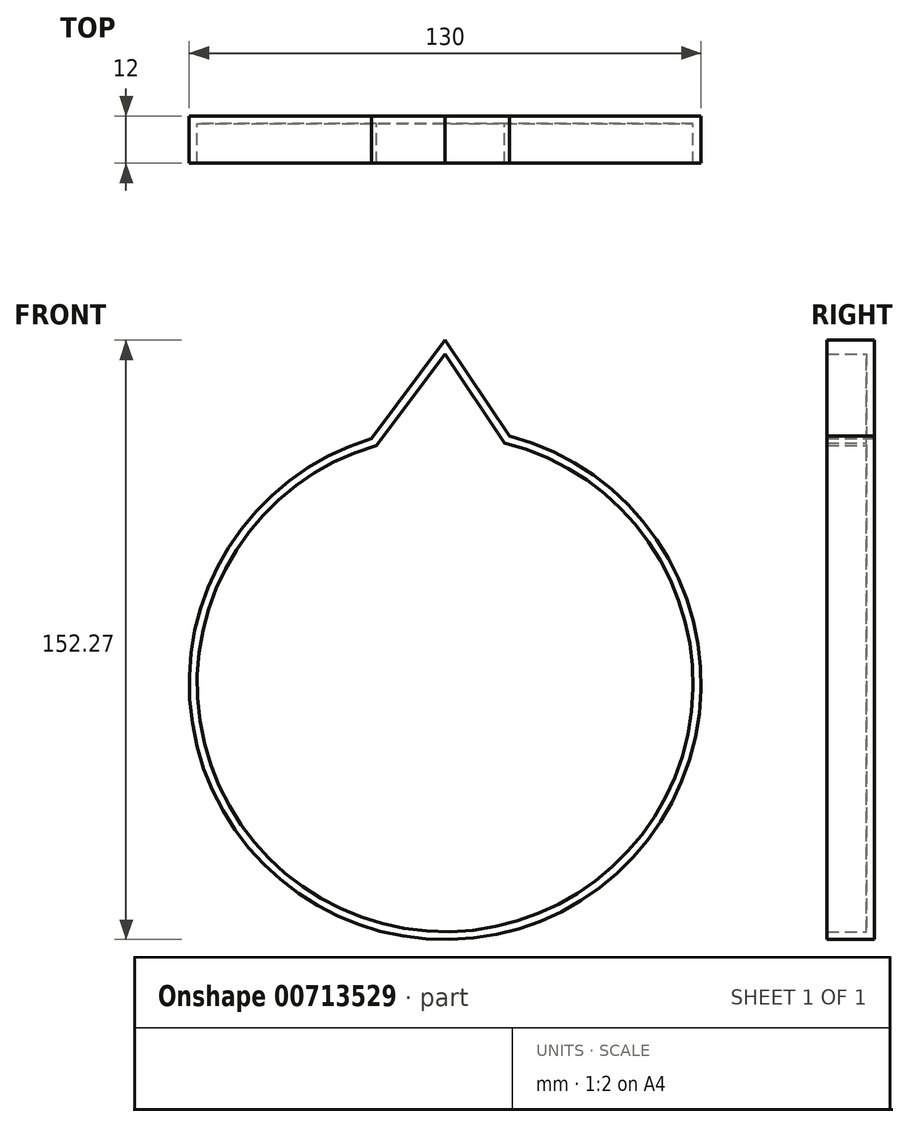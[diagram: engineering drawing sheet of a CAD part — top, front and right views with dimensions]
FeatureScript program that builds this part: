
annotation { "Feature Type Name" : "Feature", "Feature Type Description" : "" }
export const myFeature = defineFeature(function(context is Context, id is Id, definition is map)
    precondition{}
    {
        {
            var Q0;
            Q0=qCreatedBy(makeId("Front.planeOp"),FACE);
            var sketch = newSketch(context, id + "F0", { "sketchPlane" : qUnion([Q0])});
            skArc(sketch, "E0", {"start": v(-18.65, 62.27) * mm, "mid": v(1.2, -64.99) * mm, "end": v(16.35, 62.9) * mm});
            skLineSegment(sketch, "E1", {"start": v(0, 0) * mm, "end": v(0, 87.27) * mm, "construction": true});
            skLineSegment(sketch, "E2", {"start": v(0, 87.27) * mm, "end": v(-18.65, 62.27) * mm});
            skLineSegment(sketch, "E3", {"start": v(16.35, 62.9) * mm, "end": v(0, 87.27) * mm});
            skSolve(sketch);
        }
        {
            var Q0;
            Q0 = qSketchRegion(id + "F0", true);
            extrude(context, id + "F1", {"entities" : qUnion([Q0]), "depth" : 12 * mm, "offsetDistance" : 25 * mm});
        }
        {
            var Q0;
            Q0=makeQuery(id+"F1.opExtrude","CAP_FACE",FACE,{"disambiguationData":[OSD([sQuery(id+"F0.wireOp",EDGE,"E0"),sQuery(id+"F0.wireOp",EDGE,"E2"),sQuery(id+"F0.wireOp",EDGE,"E3")])],"isStart":false});
            shell(context, id + "F2", {"entities" : qUnion([Q0]), "thickness" : 2 * mm});
        }
    });
